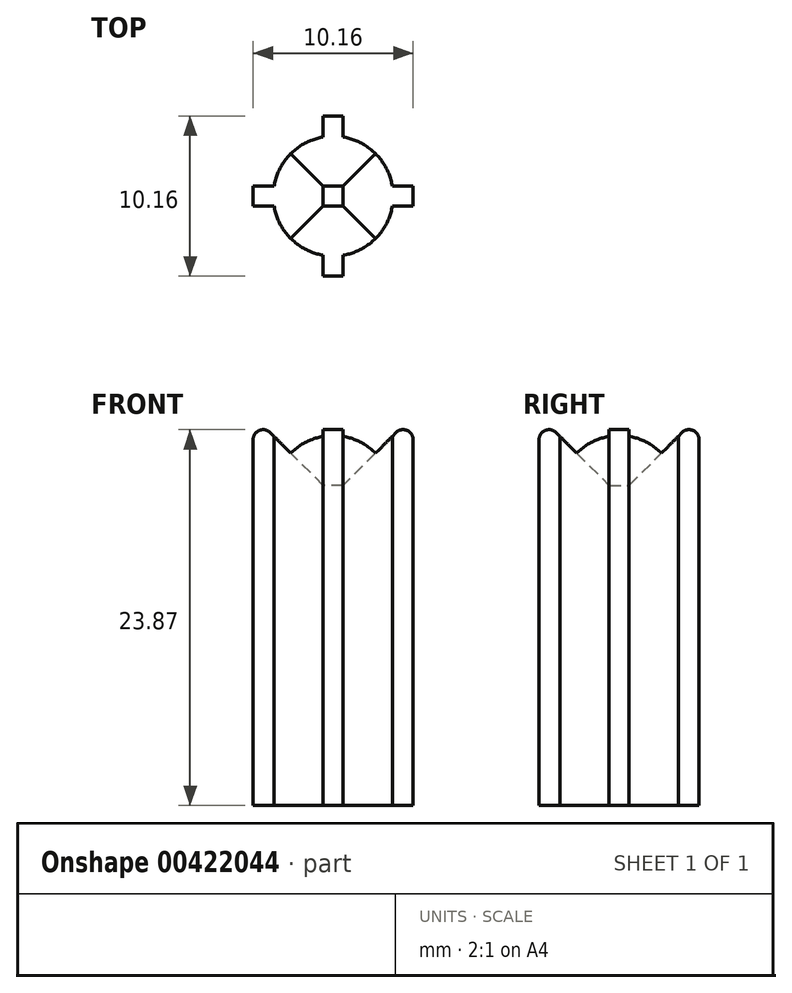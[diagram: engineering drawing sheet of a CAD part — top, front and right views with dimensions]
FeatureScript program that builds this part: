
annotation { "Feature Type Name" : "Feature", "Feature Type Description" : "" }
export const myFeature = defineFeature(function(context is Context, id is Id, definition is map)
    precondition{}
    {
        {
            var Q0;
            Q0=qCreatedBy(makeId("Top.planeOp"),FACE);
            var sketch = newSketch(context, id + "F0", { "sketchPlane" : qUnion([Q0])});
            skCircle(sketch, "E0", {"center": v(0, 0) * mm, "radius": 3.8 * mm});
            skLineSegment(sketch, "E1.bottom", {"start": v(5.08, 0.63) * mm, "end": v(-5.08, 0.63) * mm});
            skLineSegment(sketch, "E1.top", {"start": v(5.08, -0.64) * mm, "end": v(-5.08, -0.64) * mm});
            skLineSegment(sketch, "E1.left", {"start": v(5.08, 0.63) * mm, "end": v(5.08, -0.64) * mm});
            skLineSegment(sketch, "E1.right", {"start": v(-5.08, 0.63) * mm, "end": v(-5.08, -0.64) * mm});
            skLineSegment(sketch, "E2.bottom", {"start": v(0.64, 5.08) * mm, "end": v(-0.64, 5.08) * mm});
            skLineSegment(sketch, "E2.top", {"start": v(0.64, -5.08) * mm, "end": v(-0.64, -5.08) * mm});
            skLineSegment(sketch, "E2.left", {"start": v(0.64, 5.08) * mm, "end": v(0.64, -5.08) * mm});
            skLineSegment(sketch, "E2.right", {"start": v(-0.64, 5.08) * mm, "end": v(-0.64, -5.08) * mm});
            skSolve(sketch);
        }
        {
            var Q0;
            Q0 = qSketchRegion(id + "F0", true);
            extrude(context, id + "F1", {"entities" : qUnion([Q0]), "depth" : 25.4 * mm});
        }
        {
            var Q0;
            {var subQ0=sQuery(id+"F0.wireOp",EDGE,"E1.bottom");Q0=makeQuery(id+"F1.opExtrude","CAP_EDGE",EDGE,{"disambiguationData":[OSD([subQ0]),TDD([makeQuery(id+"F0.imprint","IMPRINT",EDGE,{"disambiguationData":[TD([[makeQuery(id+"F0.imprint","INTERSECT",VERTEX,{"derivedFrom":[subQ0,sQuery(id+"F0.wireOp",EDGE,"E2.left")]}),-1.0]])],"derivedFrom":subQ0})])],"isStart":false});}
            var Q1;
            {var subQ0=sQuery(id+"F0.wireOp",EDGE,"E2.right");Q1=makeQuery(id+"F1.opExtrude","CAP_EDGE",EDGE,{"disambiguationData":[OSD([subQ0]),TDD([makeQuery(id+"F0.imprint","IMPRINT",EDGE,{"disambiguationData":[TD([[makeQuery(id+"F0.imprint","INTERSECT",VERTEX,{"derivedFrom":[sQuery(id+"F0.wireOp",EDGE,"E1.bottom"),subQ0]}),-1.0]])],"derivedFrom":subQ0})])],"isStart":false});}
            var Q2;
            {var subQ0=sQuery(id+"F0.wireOp",EDGE,"E1.top");Q2=makeQuery(id+"F1.opExtrude","CAP_EDGE",EDGE,{"disambiguationData":[OSD([subQ0]),TDD([makeQuery(id+"F0.imprint","IMPRINT",EDGE,{"disambiguationData":[TD([[makeQuery(id+"F0.imprint","INTERSECT",VERTEX,{"derivedFrom":[subQ0,sQuery(id+"F0.wireOp",EDGE,"E2.left")]}),-1.0]])],"derivedFrom":subQ0})])],"isStart":false});}
            var Q3;
            {var subQ0=sQuery(id+"F0.wireOp",EDGE,"E2.left");Q3=makeQuery(id+"F1.opExtrude","CAP_EDGE",EDGE,{"disambiguationData":[OSD([subQ0]),TDD([makeQuery(id+"F0.imprint","IMPRINT",EDGE,{"disambiguationData":[TD([[makeQuery(id+"F0.imprint","INTERSECT",VERTEX,{"derivedFrom":[sQuery(id+"F0.wireOp",EDGE,"E1.bottom"),subQ0]}),-1.0]])],"derivedFrom":subQ0})])],"isStart":false});}
            chamfer(context, id + "F2", {"entities" : qUnion([Q0, Q1, Q2, Q3]), "width" : 5.08 * mm, "tangentPropagation" : true});
        }
        {
            var Q0;
            {var subQ0=sQuery(id+"F0.wireOp",EDGE,"E2.left");Q0=makeQuery(id+"F2.opChamfer","BLEND_EDGE",EDGE,{"blendedFrom":[makeQuery(id+"F1.opExtrude","CAP_EDGE",EDGE,{"disambiguationData":[OSD([subQ0]),TDD([makeQuery(id+"F0.imprint","IMPRINT",EDGE,{"disambiguationData":[TD([[makeQuery(id+"F0.imprint","INTERSECT",VERTEX,{"derivedFrom":[sQuery(id+"F0.wireOp",EDGE,"E1.bottom"),subQ0]}),-1.0]])],"derivedFrom":subQ0})])],"isStart":false}),makeQuery(id+"F1.opExtrude","SWEPT_FACE",FACE,{"disambiguationData":[OSD([sQuery(id+"F0.wireOp",EDGE,"E1.left")])]})],"blendedInto":[makeQuery(id+"F1.opExtrude","SWEPT_FACE",FACE,{"disambiguationData":[OSD([sQuery(id+"F0.wireOp",EDGE,"E1.left")])]})]});}
            var Q1;
            {var subQ0=sQuery(id+"F0.wireOp",EDGE,"E1.bottom");Q1=makeQuery(id+"F2.opChamfer","BLEND_EDGE",EDGE,{"blendedFrom":[makeQuery(id+"F1.opExtrude","CAP_EDGE",EDGE,{"disambiguationData":[OSD([subQ0]),TDD([makeQuery(id+"F0.imprint","IMPRINT",EDGE,{"disambiguationData":[TD([[makeQuery(id+"F0.imprint","INTERSECT",VERTEX,{"derivedFrom":[subQ0,sQuery(id+"F0.wireOp",EDGE,"E2.left")]}),-1.0]])],"derivedFrom":subQ0})])],"isStart":false}),makeQuery(id+"F1.opExtrude","SWEPT_FACE",FACE,{"disambiguationData":[OSD([sQuery(id+"F0.wireOp",EDGE,"E2.bottom")])]})],"blendedInto":[makeQuery(id+"F1.opExtrude","SWEPT_FACE",FACE,{"disambiguationData":[OSD([sQuery(id+"F0.wireOp",EDGE,"E2.bottom")])]})]});}
            var Q2;
            {var subQ0=sQuery(id+"F0.wireOp",EDGE,"E2.right");Q2=makeQuery(id+"F2.opChamfer","BLEND_EDGE",EDGE,{"blendedFrom":[makeQuery(id+"F1.opExtrude","CAP_EDGE",EDGE,{"disambiguationData":[OSD([subQ0]),TDD([makeQuery(id+"F0.imprint","IMPRINT",EDGE,{"disambiguationData":[TD([[makeQuery(id+"F0.imprint","INTERSECT",VERTEX,{"derivedFrom":[sQuery(id+"F0.wireOp",EDGE,"E1.bottom"),subQ0]}),-1.0]])],"derivedFrom":subQ0})])],"isStart":false}),makeQuery(id+"F1.opExtrude","SWEPT_FACE",FACE,{"disambiguationData":[OSD([sQuery(id+"F0.wireOp",EDGE,"E1.right")])]})],"blendedInto":[makeQuery(id+"F1.opExtrude","SWEPT_FACE",FACE,{"disambiguationData":[OSD([sQuery(id+"F0.wireOp",EDGE,"E1.right")])]})]});}
            var Q3;
            {var subQ0=sQuery(id+"F0.wireOp",EDGE,"E1.top");Q3=makeQuery(id+"F2.opChamfer","BLEND_EDGE",EDGE,{"blendedFrom":[makeQuery(id+"F1.opExtrude","CAP_EDGE",EDGE,{"disambiguationData":[OSD([subQ0]),TDD([makeQuery(id+"F0.imprint","IMPRINT",EDGE,{"disambiguationData":[TD([[makeQuery(id+"F0.imprint","INTERSECT",VERTEX,{"derivedFrom":[subQ0,sQuery(id+"F0.wireOp",EDGE,"E2.left")]}),-1.0]])],"derivedFrom":subQ0})])],"isStart":false}),makeQuery(id+"F1.opExtrude","SWEPT_FACE",FACE,{"disambiguationData":[OSD([sQuery(id+"F0.wireOp",EDGE,"E2.top")])]})],"blendedInto":[makeQuery(id+"F1.opExtrude","SWEPT_FACE",FACE,{"disambiguationData":[OSD([sQuery(id+"F0.wireOp",EDGE,"E2.top")])]})]});}
            fillet(context, id + "F3", {"entities" : qUnion([Q0, Q1, Q2, Q3]), "radius" : 0.64 * mm, "tangentPropagation" : true, "allowEdgeOverflow" : false});
        }
    });
